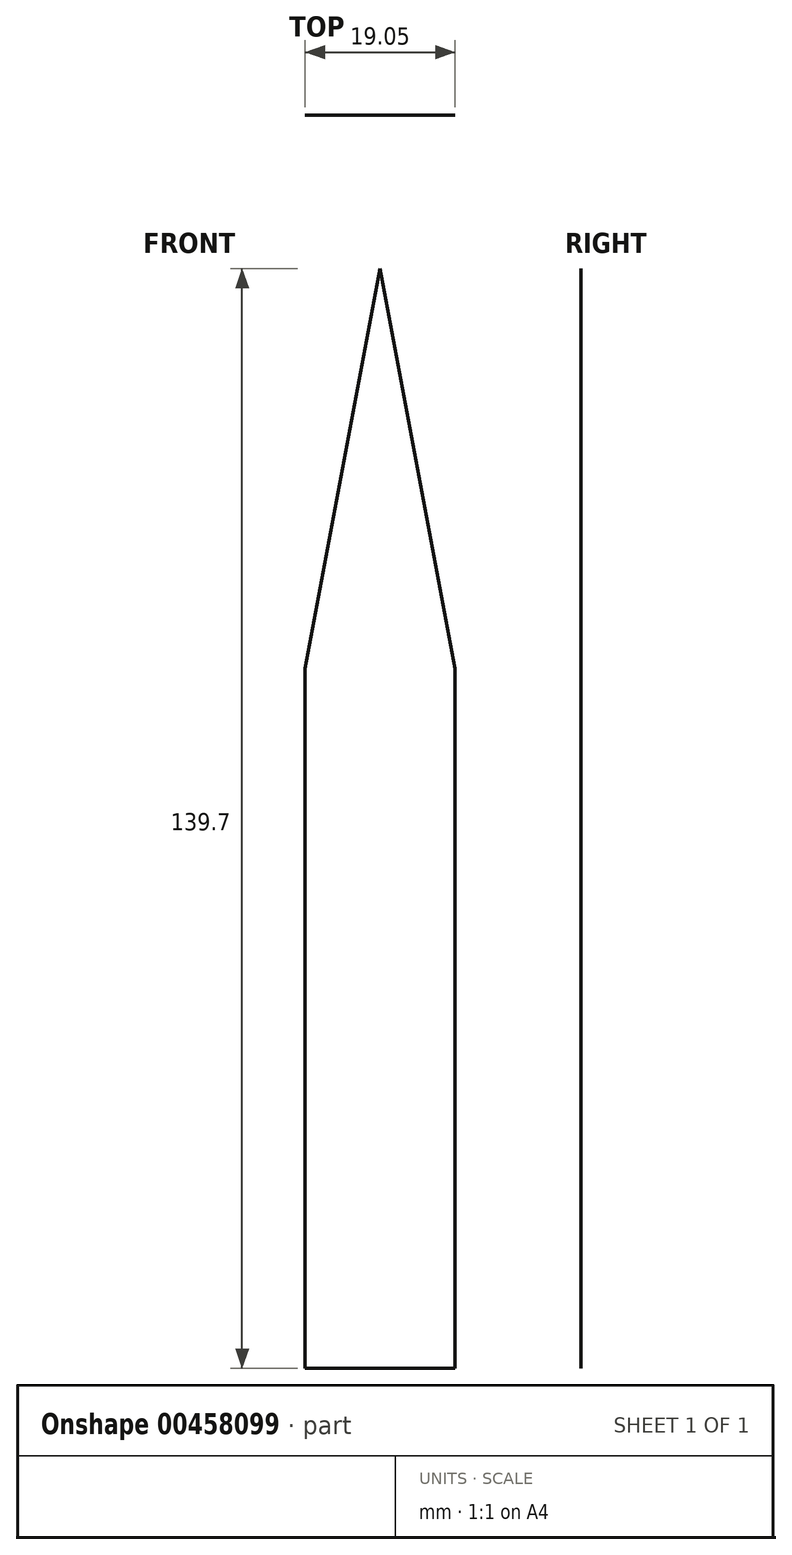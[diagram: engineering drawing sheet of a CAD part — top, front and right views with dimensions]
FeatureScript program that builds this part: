
annotation { "Feature Type Name" : "Feature", "Feature Type Description" : "" }
export const myFeature = defineFeature(function(context is Context, id is Id, definition is map)
    precondition{}
    {
        {
            var Q0;
            Q0=qCreatedBy(makeId("Front.planeOp"),FACE);
            var sketch = newSketch(context, id + "F0", { "sketchPlane" : qUnion([Q0])});
            skLineSegment(sketch, "E0", {"start": v(0, 0) * mm, "end": v(19.05, 0) * mm});
            skLineSegment(sketch, "E1", {"start": v(19.05, 0) * mm, "end": v(19.05, 139.7) * mm});
            skLineSegment(sketch, "E2", {"start": v(19.05, 139.7) * mm, "end": v(0, 139.7) * mm});
            skLineSegment(sketch, "E3", {"start": v(0, 139.7) * mm, "end": v(0, 0) * mm});
            skLineSegment(sketch, "E4", {"start": v(19.05, 88.9) * mm, "end": v(9.53, 139.7) * mm});
            skLineSegment(sketch, "E5", {"start": v(9.53, 139.7) * mm, "end": v(0, 88.9) * mm});
            skSolve(sketch);
        }
        {
            var Q0;
            {var subQ2=sQuery(id+"F0.wireOp",EDGE,"E0");Q0=makeQuery(id+"F0.imprint","IMPRINT",FACE,{"disambiguationData":[TD([[makeQuery(id+"F0.imprint","IMPRINT",EDGE,{"derivedFrom":subQ2}),1.0]])]});}
            var Q1;
            {var subQ3=sQuery(id+"F0.wireOp",EDGE,"E5");Q1=makeQuery(id+"F0.imprint","IMPRINT",FACE,{"disambiguationData":[TD([[makeQuery(id+"F0.imprint","IMPRINT",EDGE,{"derivedFrom":subQ3}),-1.0]])]});}
            var Q2;
            {var subQ3=sQuery(id+"F0.wireOp",EDGE,"E4");Q2=makeQuery(id+"F0.imprint","IMPRINT",FACE,{"disambiguationData":[TD([[makeQuery(id+"F0.imprint","IMPRINT",EDGE,{"derivedFrom":subQ3}),-1.0]])]});}
            extrude(context, id + "F1", {"entities" : qUnion([Q0, Q1, Q2]), "depth" : 1 / 203.2 * mm});
        }
        {
            var Q0;
            Q0=makeQuery(id+"F1.opExtrude","CAP_FACE",FACE,{"disambiguationData":[OSD([sQuery(id+"F0.wireOp",EDGE,"E0"),sQuery(id+"F0.wireOp",EDGE,"E1"),sQuery(id+"F0.wireOp",EDGE,"E2"),sQuery(id+"F0.wireOp",EDGE,"E3")])],"isStart":false});
            var sketch = newSketch(context, id + "F2", { "sketchPlane" : qUnion([Q0])});
            skLineSegment(sketch, "E6", {"start": v(0, 88.9) * mm, "end": v(9.53, 139.7) * mm});
            skLineSegment(sketch, "E7", {"start": v(9.53, 139.7) * mm, "end": v(19.05, 88.9) * mm});
            skSolve(sketch);
        }
        {
            var Q0;
            {var subQ0=sQuery(id+"F2.wireOp",EDGE,"E6");Q0=makeQuery(id+"F2.imprint","IMPRINT",FACE,{"disambiguationData":[TD([[makeQuery(id+"F2.imprint","IMPRINT",EDGE,{"derivedFrom":subQ0}),1.0]])]});}
            var Q1;
            {var subQ0=sQuery(id+"F2.wireOp",EDGE,"E7");Q1=makeQuery(id+"F2.imprint","IMPRINT",FACE,{"disambiguationData":[TD([[makeQuery(id+"F2.imprint","IMPRINT",EDGE,{"derivedFrom":subQ0}),1.0]])]});}
            extrude(context, id + "F3", {"entities" : qUnion([Q0, Q1]), "operationType" : NewBodyOperationType.REMOVE, "oppositeDirection" : true, "depth" : 25.4 * mm});
        }
    });
